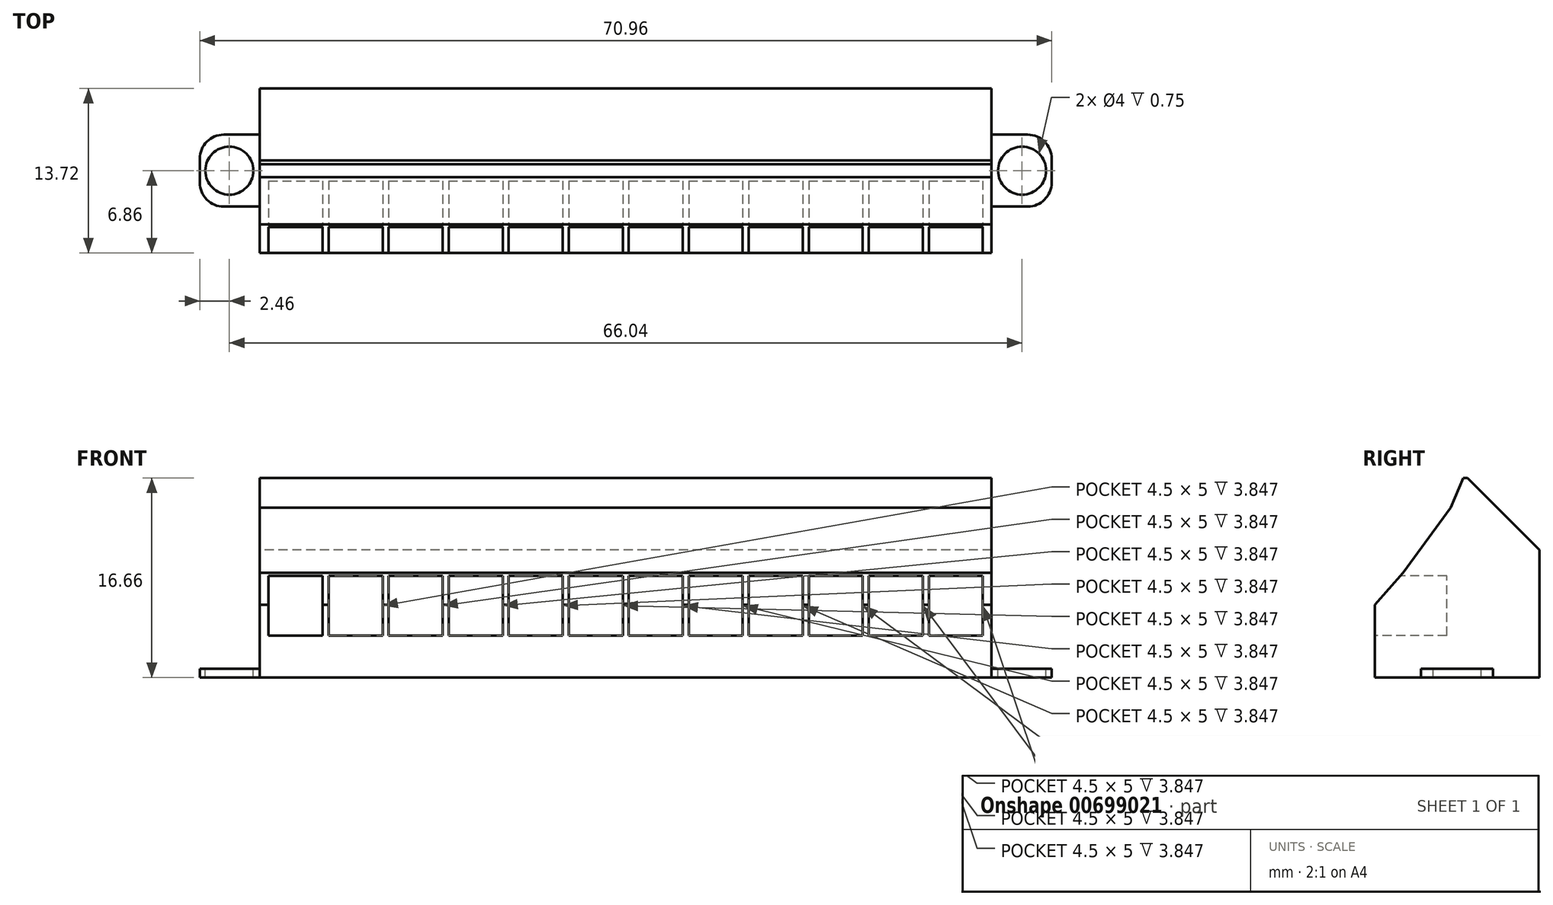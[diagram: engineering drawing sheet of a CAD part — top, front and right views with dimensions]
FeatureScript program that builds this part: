
annotation { "Feature Type Name" : "Feature", "Feature Type Description" : "" }
export const myFeature = defineFeature(function(context is Context, id is Id, definition is map)
    precondition{}
    {
        {
            var Q0;
            Q0=qCreatedBy(makeId("Top.planeOp"),FACE);
            var sketch = newSketch(context, id + "F0", { "sketchPlane" : qUnion([Q0])});
            skLineSegment(sketch, "E0.bottom", {"start": v(30.48, -6.86) * mm, "end": v(-30.48, -6.86) * mm});
            skLineSegment(sketch, "E0.top", {"start": v(30.48, 6.86) * mm, "end": v(-30.48, 6.86) * mm});
            skLineSegment(sketch, "E0.left", {"start": v(30.48, -6.86) * mm, "end": v(30.48, 6.86) * mm});
            skLineSegment(sketch, "E0.right", {"start": v(-30.48, -6.86) * mm, "end": v(-30.48, 6.86) * mm});
            skPoint(sketch, "E0.middle", {"position": v(0, 0) * mm});
            skSolve(sketch);
        }
        {
            var Q0;
            Q0 = qSketchRegion(id + "F0", true);
            extrude(context, id + "F1", {"entities" : qUnion([Q0]), "depth" : 16.66 * mm, "offsetDistance" : 25 * mm});
        }
        {
            var Q0;
            Q0=makeQuery(id+"F1.opExtrude","SWEPT_FACE",FACE,{"disambiguationData":[OSD([sQuery(id+"F0.wireOp",EDGE,"E0.right")])]});
            var sketch = newSketch(context, id + "F2", { "sketchPlane" : qUnion([Q0])});
            skLineSegment(sketch, "E1", {"start": v(-0.86, 16.66) * mm, "end": v(-6.86, 10.66) * mm});
            skLineSegment(sketch, "E2", {"start": v(-0.53, 16.66) * mm, "end": v(0.54, 14.16) * mm});
            skLineSegment(sketch, "E3", {"start": v(0.54, 14.16) * mm, "end": v(4.5, 8.74) * mm});
            skLineSegment(sketch, "E4", {"start": v(4.5, 8.74) * mm, "end": v(6.86, 6.08) * mm});
            skSolve(sketch);
        }
        {
            var Q0;
            {var subQ0=sQuery(id+"F2.wireOp",EDGE,"E1");Q0=makeQuery(id+"F2.imprint","IMPRINT",FACE,{"disambiguationData":[TD([[makeQuery(id+"F2.imprint","IMPRINT",EDGE,{"derivedFrom":subQ0}),-1.0]])]});}
            var Q1;
            {var subQ5=sQuery(id+"F2.wireOp",EDGE,"E2");Q1=makeQuery(id+"F2.imprint","IMPRINT",FACE,{"disambiguationData":[TD([[makeQuery(id+"F2.imprint","IMPRINT",EDGE,{"derivedFrom":subQ5}),1.0]])]});}
            extrude(context, id + "F3", {"entities" : qUnion([Q0, Q1]), "operationType" : NewBodyOperationType.REMOVE, "endBound" : BoundingType.THROUGH_ALL, "oppositeDirection" : true, "depth" : 25 * mm, "offsetDistance" : 25 * mm});
        }
        {
            var Q0;
            Q0=makeQuery(id+"F1.opExtrude","SWEPT_FACE",FACE,{"disambiguationData":[OSD([sQuery(id+"F0.wireOp",EDGE,"E0.top")])]});
            var sketch = newSketch(context, id + "F4", { "sketchPlane" : qUnion([Q0])});
            skCircle(sketch, "E5", {"center": v(27.5, 5.33) * mm, "radius": 2.25 * mm});
            skPoint(sketch, "E5.centerSnap0", {"position": v(30.48, 5.33) * mm});
            skCircle(sketch, "E6.1.0.0", {"center": v(22.5, 5.33) * mm, "radius": 2.25 * mm});
            skCircle(sketch, "E6.2.0.0", {"center": v(17.5, 5.33) * mm, "radius": 2.25 * mm});
            skCircle(sketch, "E6.3.0.0", {"center": v(12.5, 5.33) * mm, "radius": 2.25 * mm});
            skCircle(sketch, "E6.4.0.0", {"center": v(7.5, 5.33) * mm, "radius": 2.25 * mm});
            skCircle(sketch, "E6.5.0.0", {"center": v(2.5, 5.33) * mm, "radius": 2.25 * mm});
            skCircle(sketch, "E6.6.0.0", {"center": v(-2.5, 5.33) * mm, "radius": 2.25 * mm});
            skCircle(sketch, "E6.7.0.0", {"center": v(-7.5, 5.33) * mm, "radius": 2.25 * mm});
            skCircle(sketch, "E6.8.0.0", {"center": v(-12.5, 5.33) * mm, "radius": 2.25 * mm});
            skCircle(sketch, "E6.9.0.0", {"center": v(-17.5, 5.33) * mm, "radius": 2.25 * mm});
            skCircle(sketch, "E6.10.0.0", {"center": v(-22.5, 5.33) * mm, "radius": 2.25 * mm});
            skCircle(sketch, "E6.11.0.0", {"center": v(-27.5, 5.33) * mm, "radius": 2.25 * mm});
            skLineSegment(sketch, "E6.direction1", {"start": v(27.5, 5.33) * mm, "end": v(22.5, 5.33) * mm, "construction": true});
            skSolve(sketch);
        }
        {
            var Q0;
            Q0=makeQuery(id+"F1.opExtrude","SWEPT_FACE",FACE,{"disambiguationData":[OSD([sQuery(id+"F0.wireOp",EDGE,"E0.bottom")])]});
            var sketch = newSketch(context, id + "F5", { "sketchPlane" : qUnion([Q0])});
            skLineSegment(sketch, "E7.bottom", {"start": v(-29.75, 3.5) * mm, "end": v(-25.25, 3.5) * mm});
            skLineSegment(sketch, "E7.top", {"start": v(-29.75, 8.5) * mm, "end": v(-25.25, 8.5) * mm});
            skLineSegment(sketch, "E7.left", {"start": v(-29.75, 3.5) * mm, "end": v(-29.75, 8.5) * mm});
            skLineSegment(sketch, "E7.right", {"start": v(-25.25, 3.5) * mm, "end": v(-25.25, 8.5) * mm});
            skLineSegment(sketch, "E8.1.0.0", {"start": v(-24.75, 3.5) * mm, "end": v(-20.25, 3.5) * mm});
            skLineSegment(sketch, "E8.1.0.1", {"start": v(-24.75, 3.5) * mm, "end": v(-24.75, 8.5) * mm});
            skLineSegment(sketch, "E8.1.0.2", {"start": v(-20.25, 3.5) * mm, "end": v(-20.25, 8.5) * mm});
            skLineSegment(sketch, "E8.1.0.3", {"start": v(-24.75, 8.5) * mm, "end": v(-20.25, 8.5) * mm});
            skLineSegment(sketch, "E8.2.0.0", {"start": v(-19.75, 3.5) * mm, "end": v(-15.25, 3.5) * mm});
            skLineSegment(sketch, "E8.2.0.1", {"start": v(-19.75, 3.5) * mm, "end": v(-19.75, 8.5) * mm});
            skLineSegment(sketch, "E8.2.0.2", {"start": v(-15.25, 3.5) * mm, "end": v(-15.25, 8.5) * mm});
            skLineSegment(sketch, "E8.2.0.3", {"start": v(-19.75, 8.5) * mm, "end": v(-15.25, 8.5) * mm});
            skLineSegment(sketch, "E8.3.0.0", {"start": v(-14.75, 3.5) * mm, "end": v(-10.25, 3.5) * mm});
            skLineSegment(sketch, "E8.3.0.1", {"start": v(-14.75, 3.5) * mm, "end": v(-14.75, 8.5) * mm});
            skLineSegment(sketch, "E8.3.0.2", {"start": v(-10.25, 3.5) * mm, "end": v(-10.25, 8.5) * mm});
            skLineSegment(sketch, "E8.3.0.3", {"start": v(-14.75, 8.5) * mm, "end": v(-10.25, 8.5) * mm});
            skLineSegment(sketch, "E8.4.0.0", {"start": v(-9.75, 3.5) * mm, "end": v(-5.25, 3.5) * mm});
            skLineSegment(sketch, "E8.4.0.1", {"start": v(-9.75, 3.5) * mm, "end": v(-9.75, 8.5) * mm});
            skLineSegment(sketch, "E8.4.0.2", {"start": v(-5.25, 3.5) * mm, "end": v(-5.25, 8.5) * mm});
            skLineSegment(sketch, "E8.4.0.3", {"start": v(-9.75, 8.5) * mm, "end": v(-5.25, 8.5) * mm});
            skLineSegment(sketch, "E8.5.0.0", {"start": v(-4.75, 3.5) * mm, "end": v(-0.25, 3.5) * mm});
            skLineSegment(sketch, "E8.5.0.1", {"start": v(-4.75, 3.5) * mm, "end": v(-4.75, 8.5) * mm});
            skLineSegment(sketch, "E8.5.0.2", {"start": v(-0.25, 3.5) * mm, "end": v(-0.25, 8.5) * mm});
            skLineSegment(sketch, "E8.5.0.3", {"start": v(-4.75, 8.5) * mm, "end": v(-0.25, 8.5) * mm});
            skLineSegment(sketch, "E8.6.0.0", {"start": v(0.25, 3.5) * mm, "end": v(4.75, 3.5) * mm});
            skLineSegment(sketch, "E8.6.0.1", {"start": v(0.25, 3.5) * mm, "end": v(0.25, 8.5) * mm});
            skLineSegment(sketch, "E8.6.0.2", {"start": v(4.75, 3.5) * mm, "end": v(4.75, 8.5) * mm});
            skLineSegment(sketch, "E8.6.0.3", {"start": v(0.25, 8.5) * mm, "end": v(4.75, 8.5) * mm});
            skLineSegment(sketch, "E8.7.0.0", {"start": v(5.25, 3.5) * mm, "end": v(9.75, 3.5) * mm});
            skLineSegment(sketch, "E8.7.0.1", {"start": v(5.25, 3.5) * mm, "end": v(5.25, 8.5) * mm});
            skLineSegment(sketch, "E8.7.0.2", {"start": v(9.75, 3.5) * mm, "end": v(9.75, 8.5) * mm});
            skLineSegment(sketch, "E8.7.0.3", {"start": v(5.25, 8.5) * mm, "end": v(9.75, 8.5) * mm});
            skLineSegment(sketch, "E8.8.0.0", {"start": v(10.25, 3.5) * mm, "end": v(14.75, 3.5) * mm});
            skLineSegment(sketch, "E8.8.0.1", {"start": v(10.25, 3.5) * mm, "end": v(10.25, 8.5) * mm});
            skLineSegment(sketch, "E8.8.0.2", {"start": v(14.75, 3.5) * mm, "end": v(14.75, 8.5) * mm});
            skLineSegment(sketch, "E8.8.0.3", {"start": v(10.25, 8.5) * mm, "end": v(14.75, 8.5) * mm});
            skLineSegment(sketch, "E8.9.0.0", {"start": v(15.25, 3.5) * mm, "end": v(19.75, 3.5) * mm});
            skLineSegment(sketch, "E8.9.0.1", {"start": v(15.25, 3.5) * mm, "end": v(15.25, 8.5) * mm});
            skLineSegment(sketch, "E8.9.0.2", {"start": v(19.75, 3.5) * mm, "end": v(19.75, 8.5) * mm});
            skLineSegment(sketch, "E8.9.0.3", {"start": v(15.25, 8.5) * mm, "end": v(19.75, 8.5) * mm});
            skLineSegment(sketch, "E8.10.0.0", {"start": v(20.25, 3.5) * mm, "end": v(24.75, 3.5) * mm});
            skLineSegment(sketch, "E8.10.0.1", {"start": v(20.25, 3.5) * mm, "end": v(20.25, 8.5) * mm});
            skLineSegment(sketch, "E8.10.0.2", {"start": v(24.75, 3.5) * mm, "end": v(24.75, 8.5) * mm});
            skLineSegment(sketch, "E8.10.0.3", {"start": v(20.25, 8.5) * mm, "end": v(24.75, 8.5) * mm});
            skLineSegment(sketch, "E8.11.0.0", {"start": v(25.25, 3.5) * mm, "end": v(29.75, 3.5) * mm});
            skLineSegment(sketch, "E8.11.0.1", {"start": v(25.25, 3.5) * mm, "end": v(25.25, 8.5) * mm});
            skLineSegment(sketch, "E8.11.0.2", {"start": v(29.75, 3.5) * mm, "end": v(29.75, 8.5) * mm});
            skLineSegment(sketch, "E8.11.0.3", {"start": v(25.25, 8.5) * mm, "end": v(29.75, 8.5) * mm});
            skLineSegment(sketch, "E8.direction1", {"start": v(-29.75, 3.5) * mm, "end": v(-24.75, 3.5) * mm, "construction": true});
            skSolve(sketch);
        }
        {
            var Q0;
            Q0 = qSketchRegion(id + "F5", true);
            var Q1;
            Q1 = qSketchRegion(id + "F4", true);
            extrude(context, id + "F6", {"entities" : qUnion([Q0, Q1]), "operationType" : NewBodyOperationType.REMOVE, "oppositeDirection" : true, "depth" : 6 * mm, "offsetDistance" : 25 * mm});
        }
        {
            var Q0;
            Q0=makeQuery(id+"F3.boolean.opBoolean","COPY",FACE,{"derivedFrom":makeQuery(id+"F3.opExtrude","SWEPT_FACE",FACE,{"disambiguationData":[OSD([sQuery(id+"F2.wireOp",EDGE,"E1")])]})});
            var sketch = newSketch(context, id + "F7", { "sketchPlane" : qUnion([Q0])});
            skCircle(sketch, "E9", {"center": v(-27.5, -6.93) * mm, "radius": 2.25 * mm});
            skCircle(sketch, "E10.1.0.0", {"center": v(-22.5, -6.93) * mm, "radius": 2.25 * mm});
            skCircle(sketch, "E10.2.0.0", {"center": v(-17.5, -6.93) * mm, "radius": 2.25 * mm});
            skCircle(sketch, "E10.3.0.0", {"center": v(-12.5, -6.93) * mm, "radius": 2.25 * mm});
            skCircle(sketch, "E10.4.0.0", {"center": v(-7.5, -6.93) * mm, "radius": 2.25 * mm});
            skCircle(sketch, "E10.5.0.0", {"center": v(-2.5, -6.93) * mm, "radius": 2.25 * mm});
            skCircle(sketch, "E10.6.0.0", {"center": v(2.5, -6.93) * mm, "radius": 2.25 * mm});
            skCircle(sketch, "E10.7.0.0", {"center": v(7.5, -6.93) * mm, "radius": 2.25 * mm});
            skCircle(sketch, "E10.8.0.0", {"center": v(12.5, -6.93) * mm, "radius": 2.25 * mm});
            skCircle(sketch, "E10.9.0.0", {"center": v(17.5, -6.93) * mm, "radius": 2.25 * mm});
            skCircle(sketch, "E10.10.0.0", {"center": v(22.5, -6.93) * mm, "radius": 2.25 * mm});
            skCircle(sketch, "E10.11.0.0", {"center": v(27.5, -6.93) * mm, "radius": 2.25 * mm});
            skLineSegment(sketch, "E10.direction1", {"start": v(-27.5, -6.93) * mm, "end": v(-22.5, -6.93) * mm, "construction": true});
            skSolve(sketch);
        }
        {
            var Q0;
            Q0 = qSketchRegion(id + "F7", true);
            extrude(context, id + "F8", {"entities" : qUnion([Q0]), "operationType" : NewBodyOperationType.REMOVE, "oppositeDirection" : true, "depth" : 2 * mm, "offsetDistance" : 25 * mm});
        }
        {
            var Q0;
            Q0=makeQuery(id+"F1.opExtrude","SWEPT_FACE",FACE,{"disambiguationData":[OSD([sQuery(id+"F0.wireOp",EDGE,"E0.right")])]});
            var sketch = newSketch(context, id + "F9", { "sketchPlane" : qUnion([Q0])});
            skLineSegment(sketch, "E11.bottom", {"start": v(3, 0.75) * mm, "end": v(-3, 0.75) * mm});
            skLineSegment(sketch, "E11.top", {"start": v(3, -0.75) * mm, "end": v(-3, -0.75) * mm});
            skLineSegment(sketch, "E11.left", {"start": v(3, 0.75) * mm, "end": v(3, -0.75) * mm});
            skLineSegment(sketch, "E11.right", {"start": v(-3, 0.75) * mm, "end": v(-3, -0.75) * mm});
            skPoint(sketch, "E11.middle", {"position": v(0, 0) * mm});
            skSolve(sketch);
        }
        {
            var Q0;
            {var subQ0=sQuery(id+"F9.wireOp",EDGE,"E11.bottom");Q0=makeQuery(id+"F9.imprint","IMPRINT",FACE,{"disambiguationData":[TD([[makeQuery(id+"F9.imprint","IMPRINT",EDGE,{"derivedFrom":subQ0}),1.0]])]});}
            extrude(context, id + "F10", {"entities" : qUnion([Q0]), "operationType" : NewBodyOperationType.ADD, "depth" : 5 * mm, "offsetDistance" : 25 * mm});
        }
        {
            var Q0;
            Q0=makeQuery(id+"F1.opExtrude","SWEPT_FACE",FACE,{"disambiguationData":[OSD([sQuery(id+"F0.wireOp",EDGE,"E0.left")])]});
            var sketch = newSketch(context, id + "F11", { "sketchPlane" : qUnion([Q0])});
            skLineSegment(sketch, "E12.bottom", {"start": v(-3, -0.75) * mm, "end": v(3, -0.75) * mm});
            skLineSegment(sketch, "E12.top", {"start": v(-3, 0.75) * mm, "end": v(3, 0.75) * mm});
            skLineSegment(sketch, "E12.left", {"start": v(-3, -0.75) * mm, "end": v(-3, 0.75) * mm});
            skLineSegment(sketch, "E12.right", {"start": v(3, -0.75) * mm, "end": v(3, 0.75) * mm});
            skPoint(sketch, "E12.middle", {"position": v(0, 0) * mm});
            skSolve(sketch);
        }
        {
            var Q0;
            {var subQ0=sQuery(id+"F11.wireOp",EDGE,"E12.top");Q0=makeQuery(id+"F11.imprint","IMPRINT",FACE,{"disambiguationData":[TD([[makeQuery(id+"F11.imprint","IMPRINT",EDGE,{"derivedFrom":subQ0}),-1.0]])]});}
            extrude(context, id + "F12", {"entities" : qUnion([Q0]), "operationType" : NewBodyOperationType.ADD, "depth" : 5 * mm, "offsetDistance" : 25 * mm});
        }
        {
            var Q0;
            Q0=makeQuery(id+"F10.opExtrude","CAP_EDGE",EDGE,{"disambiguationData":[OSD([sQuery(id+"F9.wireOp",EDGE,"E11.right")])],"isStart":false});
            var Q1;
            Q1=makeQuery(id+"F10.opExtrude","CAP_EDGE",EDGE,{"disambiguationData":[OSD([sQuery(id+"F9.wireOp",EDGE,"E11.left")])],"isStart":false});
            var Q2;
            Q2=makeQuery(id+"F12.opExtrude","CAP_EDGE",EDGE,{"disambiguationData":[OSD([sQuery(id+"F11.wireOp",EDGE,"E12.left")])],"isStart":false});
            var Q3;
            Q3=makeQuery(id+"F12.opExtrude","CAP_EDGE",EDGE,{"disambiguationData":[OSD([sQuery(id+"F11.wireOp",EDGE,"E12.right")])],"isStart":false});
            fillet(context, id + "F13", {"entities" : qUnion([Q0, Q1, Q2, Q3]), "radius" : 2 * mm, "tangentPropagation" : true, "allowEdgeOverflow" : false});
        }
        {
            var Q0;
            Q0=makeQuery(id+"F10.opExtrude","SWEPT_FACE",FACE,{"disambiguationData":[OSD([sQuery(id+"F9.wireOp",EDGE,"E11.bottom")])]});
            var sketch = newSketch(context, id + "F14", { "sketchPlane" : qUnion([Q0])});
            skCircle(sketch, "E13", {"center": v(-33.02, 0) * mm, "radius": 2 * mm});
            skPoint(sketch, "E13.centerSnap0", {"position": v(-35.48, 0) * mm});
            skSolve(sketch);
        }
        {
            var Q0;
            Q0 = qSketchRegion(id + "F14", true);
            extrude(context, id + "F15", {"entities" : qUnion([Q0]), "operationType" : NewBodyOperationType.REMOVE, "endBound" : BoundingType.THROUGH_ALL, "oppositeDirection" : true, "depth" : 0.5 * mm, "offsetDistance" : 25 * mm});
        }
        {
            var Q0;
            Q0=makeQuery(id+"F12.opExtrude","SWEPT_FACE",FACE,{"disambiguationData":[OSD([sQuery(id+"F11.wireOp",EDGE,"E12.top")])]});
            var sketch = newSketch(context, id + "F16", { "sketchPlane" : qUnion([Q0])});
            skCircle(sketch, "E14", {"center": v(33.02, 0) * mm, "radius": 2 * mm});
            skPoint(sketch, "E14.centerSnap0", {"position": v(35.48, 0) * mm});
            skSolve(sketch);
        }
        {
            var Q0;
            Q0 = qSketchRegion(id + "F16", true);
            extrude(context, id + "F17", {"entities" : qUnion([Q0]), "operationType" : NewBodyOperationType.REMOVE, "endBound" : BoundingType.THROUGH_ALL, "oppositeDirection" : true, "depth" : 0.5 * mm, "offsetDistance" : 25 * mm});
        }
    });
